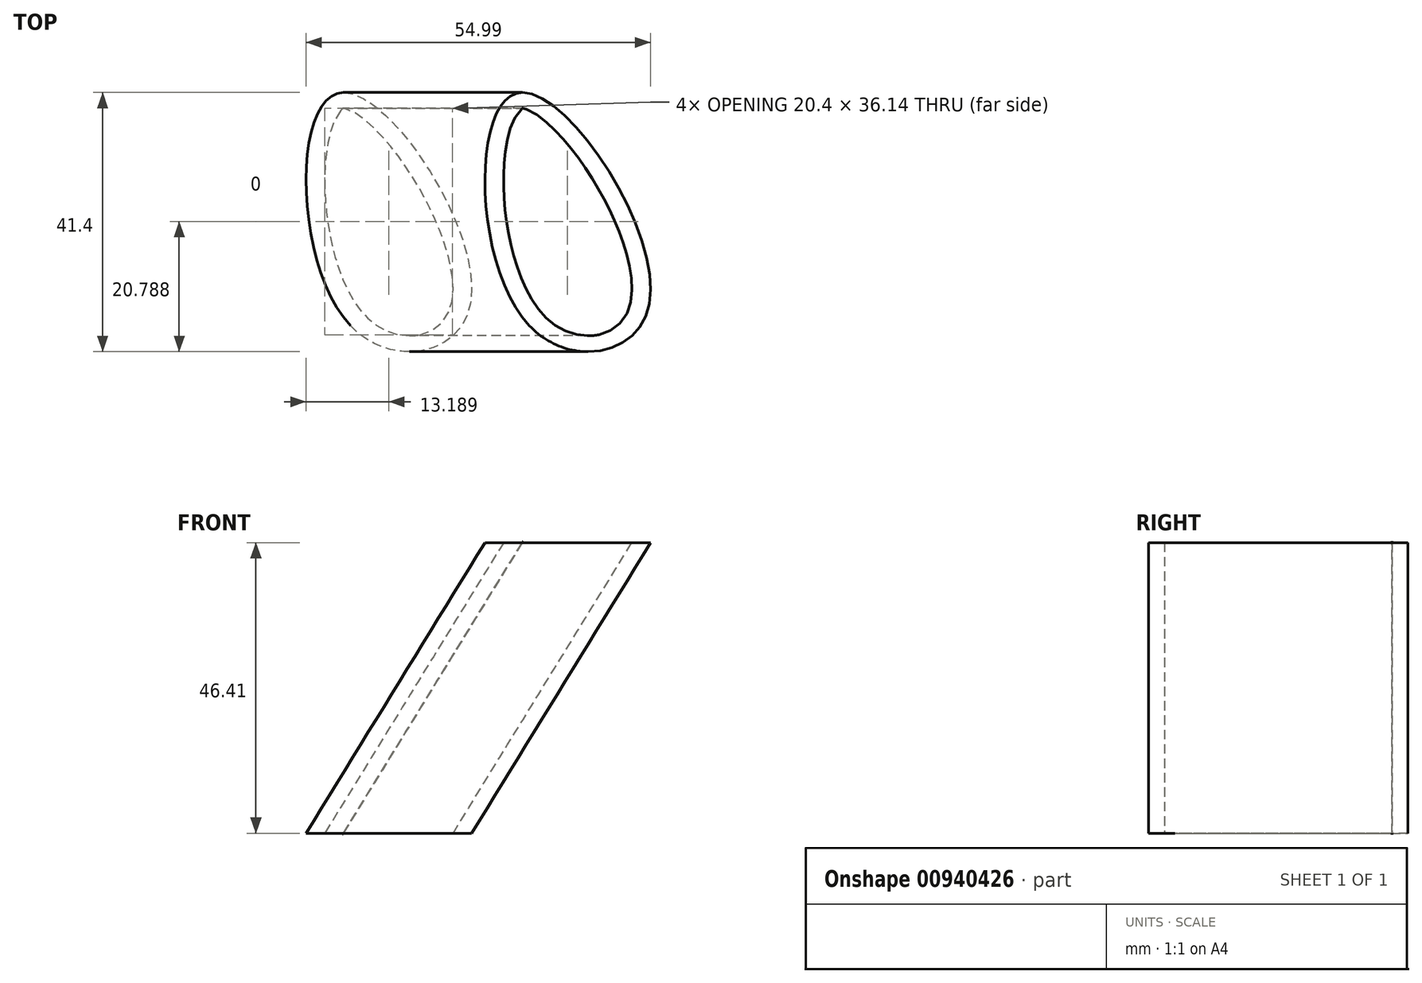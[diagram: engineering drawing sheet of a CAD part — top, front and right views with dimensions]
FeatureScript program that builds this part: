
annotation { "Feature Type Name" : "Feature", "Feature Type Description" : "" }
export const myFeature = defineFeature(function(context is Context, id is Id, definition is map)
    precondition{}
    {
        {
            var Q0;
            Q0=qCreatedBy(makeId("Top.planeOp"),FACE);
            var sketch = newSketch(context, id + "F0", { "sketchPlane" : qUnion([Q0])});
            skFitSpline(sketch, "E0", {"points": [v(0, 0) * mm, v(-1.92, 37.13) * mm, v(19.07, 3.03) * mm, v(0, 0) * mm]});
            skSolve(sketch);
        }
        {
            var Q0;
            Q0=qCreatedBy(makeId("Front.planeOp"),FACE);
            var sketch = newSketch(context, id + "F1", { "sketchPlane" : qUnion([Q0])});
            skLineSegment(sketch, "E1", {"start": v(0, 0) * mm, "end": v(28.55, 46.41) * mm});
            skSolve(sketch);
        }
        {
            var Q0;
            Q0=makeQuery(id+"F0.imprint","IMPRINT",FACE,{"disambiguationData":[TD([[makeQuery(id+"F0.imprint","IMPRINT",EDGE,{"derivedFrom":sQuery(id+"F0.wireOp",EDGE,"E0")}),-1.0]])]});
            var Q1;
            Q1=sQuery(id+"F1.wireOp",EDGE,"E1");
            sweep(context, id + "F2", {"profiles" : qUnion([Q0]), "path" : qUnion([Q1])});
        }
        {
            var Q0;
            Q0=makeQuery(id+"F2.opSweep","CAP_FACE",FACE,{"disambiguationData":[OSD([sQuery(id+"F0.wireOp",EDGE,"E0"),sQuery(id+"F1.wireOp",VERTEX,"E1.start")])],"isStart":true});
            var Q1;
            Q1=makeQuery(id+"F2.opSweep","CAP_FACE",FACE,{"disambiguationData":[OSD([sQuery(id+"F0.wireOp",EDGE,"E0"),sQuery(id+"F1.wireOp",VERTEX,"E1.end")])],"isStart":false});
            shell(context, id + "F3", {"entities" : qUnion([Q0, Q1]), "thickness" : 2.54 * mm});
        }
    });
